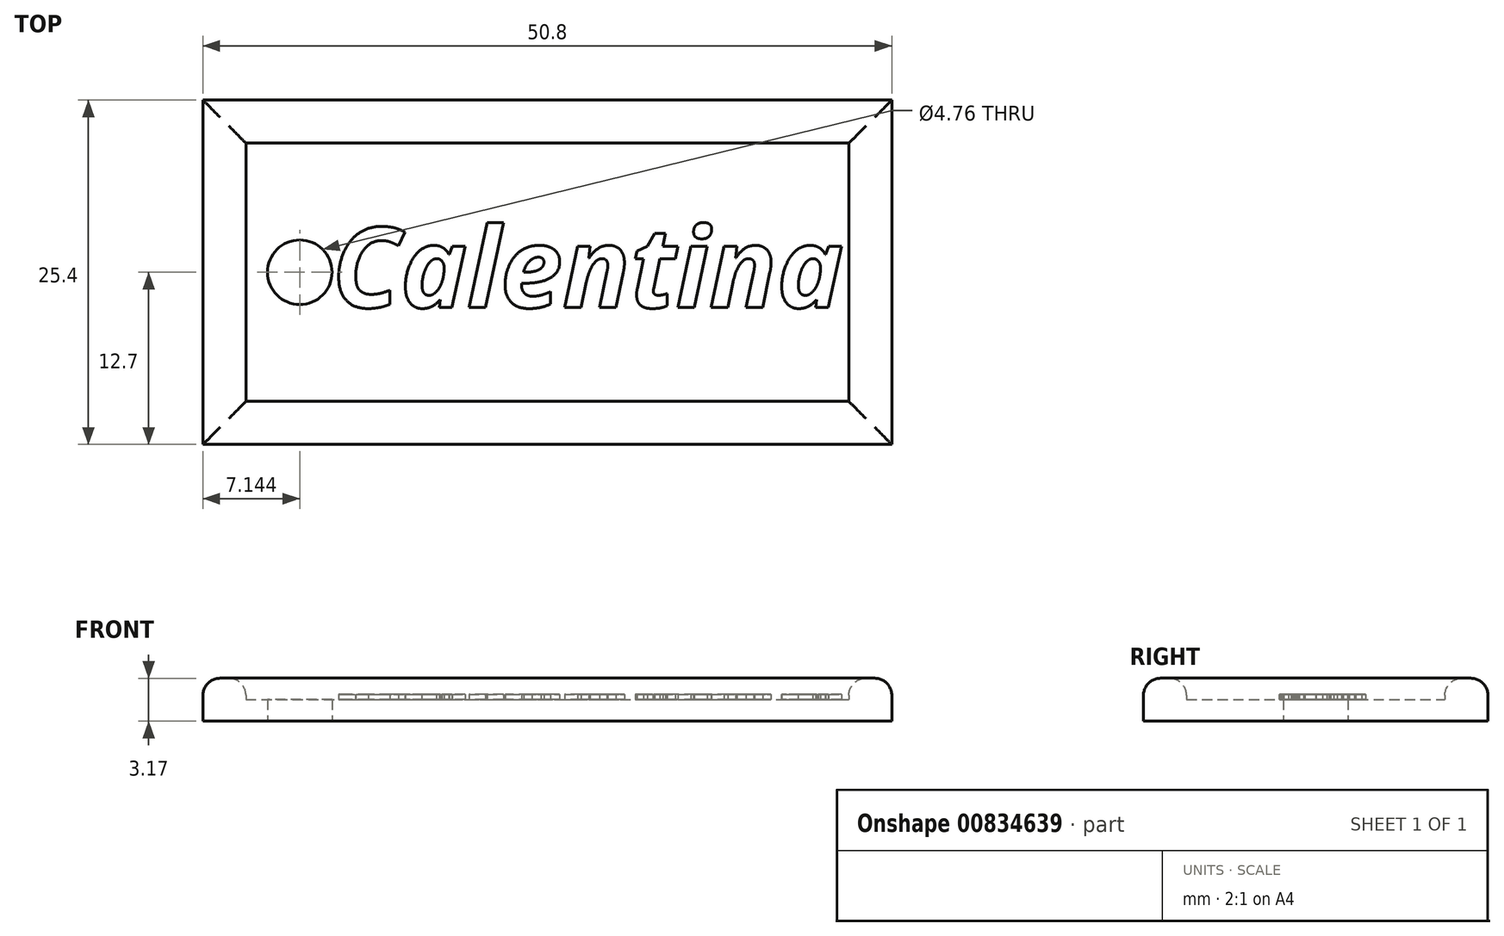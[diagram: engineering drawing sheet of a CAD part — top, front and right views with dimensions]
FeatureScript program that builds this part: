
annotation { "Feature Type Name" : "Feature", "Feature Type Description" : "" }
export const myFeature = defineFeature(function(context is Context, id is Id, definition is map)
    precondition{}
    {
        {
            var Q0;
            Q0=qCreatedBy(makeId("Top.planeOp"),FACE);
            var sketch = newSketch(context, id + "F0", { "sketchPlane" : qUnion([Q0])});
            skLineSegment(sketch, "E0.bottom", {"start": v(0, 0) * mm, "end": v(50.8, 0) * mm});
            skLineSegment(sketch, "E0.top", {"start": v(0, 25.4) * mm, "end": v(50.8, 25.4) * mm});
            skLineSegment(sketch, "E0.left", {"start": v(0, 0) * mm, "end": v(0, 25.4) * mm});
            skLineSegment(sketch, "E0.right", {"start": v(50.8, 0) * mm, "end": v(50.8, 25.4) * mm});
            skCircle(sketch, "E1", {"center": v(7.14, 12.7) * mm, "radius": 2.38 * mm});
            skPoint(sketch, "E1.centerSnap0", {"position": v(0, 12.7) * mm});
            skLineSegment(sketch, "E2.0", {"start": v(3.18, 22.23) * mm, "end": v(47.62, 22.23) * mm});
            skLineSegment(sketch, "E2.1", {"start": v(3.18, 3.18) * mm, "end": v(3.17, 22.22) * mm});
            skLineSegment(sketch, "E2.2", {"start": v(3.18, 3.18) * mm, "end": v(47.62, 3.18) * mm});
            skLineSegment(sketch, "E2.3", {"start": v(47.62, 3.18) * mm, "end": v(47.62, 22.23) * mm});
            skSolve(sketch);
        }
        {
            var Q0;
            Q0=makeQuery(id+"F0.imprint","IMPRINT",FACE,{"disambiguationData":[TD([[makeQuery(id+"F0.imprint","IMPRINT",EDGE,{"derivedFrom":sQuery(id+"F0.wireOp",EDGE,"E1")}),-1.0]])]});
            extrude(context, id + "F1", {"entities" : qUnion([Q0]), "depth" : 1.59 * mm, "offsetDistance" : 25.4 * mm});
        }
        {
            var Q0;
            Q0 = qSketchRegion(id + "F0", true);
            extrude(context, id + "F2", {"entities" : qUnion([Q0]), "operationType" : NewBodyOperationType.ADD, "depth" : 3.17 * mm, "offsetDistance" : 25.4 * mm});
        }
        {
            var Q0;
            Q0=makeQuery(id+"F2.opExtrude","CAP_EDGE",EDGE,{"disambiguationData":[OSD([sQuery(id+"F0.wireOp",EDGE,"E0.bottom")])],"isStart":false});
            var Q1;
            Q1=makeQuery(id+"F2.opExtrude","CAP_EDGE",EDGE,{"disambiguationData":[OSD([sQuery(id+"F0.wireOp",EDGE,"E0.left")])],"isStart":false});
            var Q2;
            Q2=makeQuery(id+"F2.opExtrude","CAP_EDGE",EDGE,{"disambiguationData":[OSD([sQuery(id+"F0.wireOp",EDGE,"E0.top")])],"isStart":false});
            var Q3;
            Q3=makeQuery(id+"F2.opExtrude","CAP_EDGE",EDGE,{"disambiguationData":[OSD([sQuery(id+"F0.wireOp",EDGE,"E0.right")])],"isStart":false});
            var Q4;
            Q4=makeQuery(id+"F2.opExtrude","CAP_EDGE",EDGE,{"disambiguationData":[OSD([sQuery(id+"F0.wireOp",EDGE,"E2.0")])],"isStart":false});
            var Q5;
            Q5=makeQuery(id+"F2.opExtrude","CAP_EDGE",EDGE,{"disambiguationData":[OSD([sQuery(id+"F0.wireOp",EDGE,"E2.1")])],"isStart":false});
            var Q6;
            Q6=makeQuery(id+"F2.opExtrude","CAP_EDGE",EDGE,{"disambiguationData":[OSD([sQuery(id+"F0.wireOp",EDGE,"E2.2")])],"isStart":false});
            var Q7;
            Q7=makeQuery(id+"F2.opExtrude","CAP_EDGE",EDGE,{"disambiguationData":[OSD([sQuery(id+"F0.wireOp",EDGE,"E2.3")])],"isStart":false});
            fillet(context, id + "F3", {"entities" : qUnion([Q0, Q1, Q2, Q3, Q4, Q5, Q6, Q7]), "radius" : 1.27 * mm, "tangentPropagation" : true, "allowEdgeOverflow" : false});
        }
        {
            var Q0;
            Q0=makeQuery(id+"F1.opExtrude","CAP_FACE",FACE,{"disambiguationData":[OSD([sQuery(id+"F0.wireOp",EDGE,"E1"),sQuery(id+"F0.wireOp",EDGE,"E2.0"),sQuery(id+"F0.wireOp",EDGE,"E2.1"),sQuery(id+"F0.wireOp",EDGE,"E2.2"),sQuery(id+"F0.wireOp",EDGE,"E2.3")])],"isStart":false});
            var sketch = newSketch(context, id + "F4", { "sketchPlane" : qUnion([Q0])});
            skText(sketch, "E3", { "text": "Calentina", "fontName": "OpenSans-BoldItalic.ttf"});
            const initialGuessF4  = {"E3": [0.00952, 0.0101, 1, 0, 0.00594]};
            skSetInitialGuess(sketch, initialGuessF4);
            skSolve(sketch);
        }
        {
            var Q0;
            Q0 = qSketchRegion(id + "F4", true);
            extrude(context, id + "F5", {"entities" : qUnion([Q0]), "operationType" : NewBodyOperationType.ADD, "depth" : 0.4 * mm, "offsetDistance" : 25.4 * mm});
        }
    });
